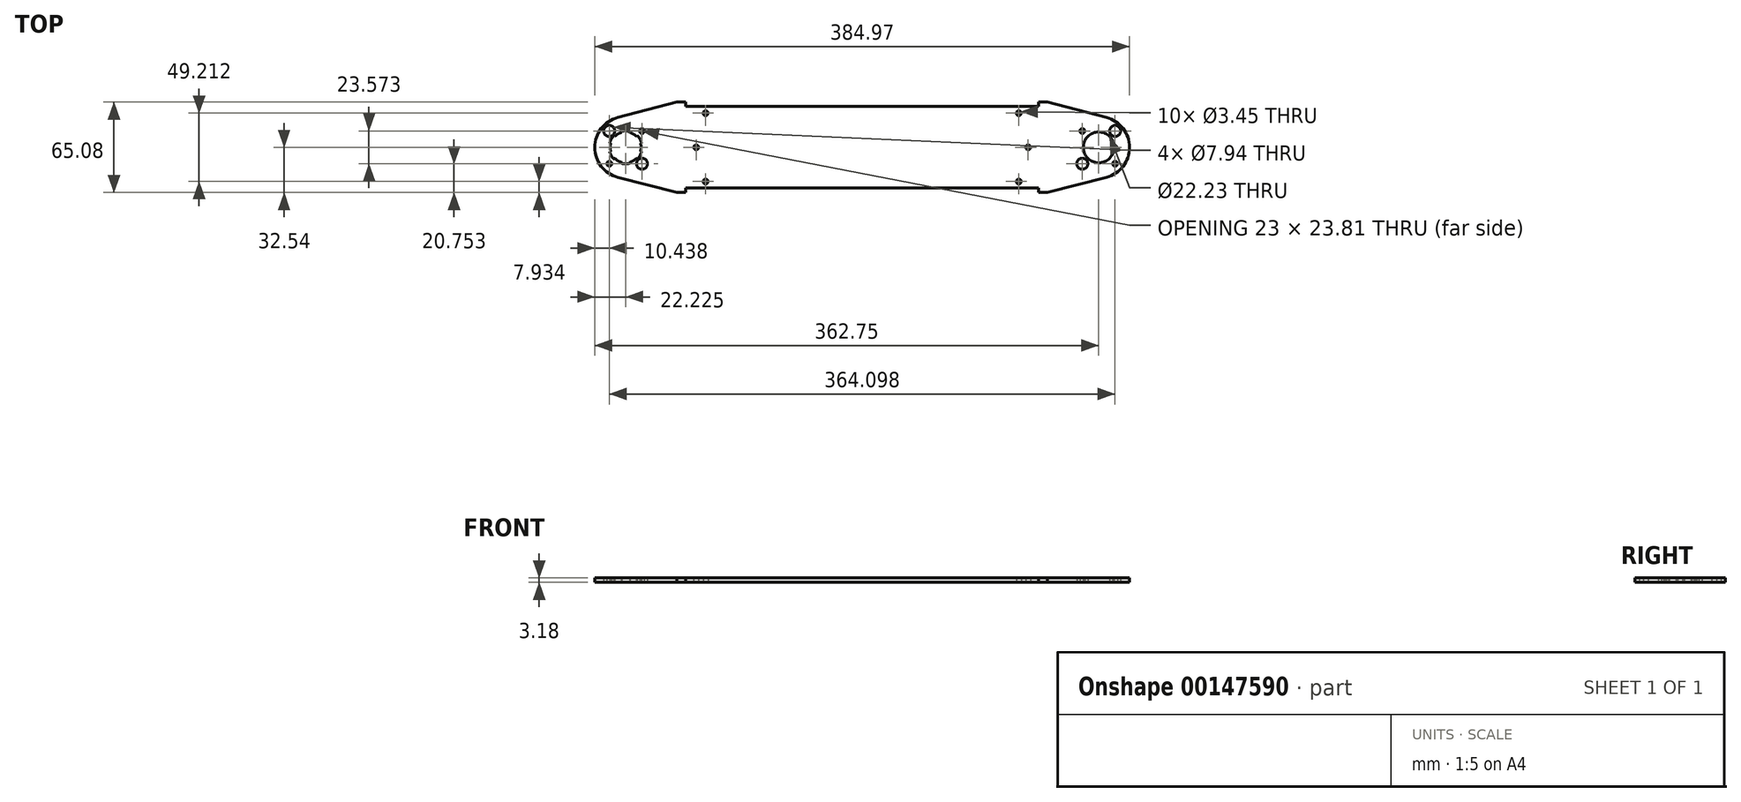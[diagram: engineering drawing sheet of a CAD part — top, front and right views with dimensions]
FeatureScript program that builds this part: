
annotation { "Feature Type Name" : "Feature", "Feature Type Description" : "" }
export const myFeature = defineFeature(function(context is Context, id is Id, definition is map)
    precondition{}
    {
        {
            var Q0;
            Q0=qCreatedBy(makeId("Top.planeOp"),FACE);
            var sketch = newSketch(context, id + "F0", { "sketchPlane" : qUnion([Q0])});
            skPoint(sketch, "E0.rect.middle", {"position": v(0, 0) * mm});
            skCircle(sketch, "E1", {"center": v(0, 0) * mm, "radius": 11.11 * mm});
            skLineSegment(sketch, "E2.bottom", {"start": v(11.79, 11.79) * mm, "end": v(-11.79, 11.79) * mm, "construction": true});
            skLineSegment(sketch, "E2.left", {"start": v(11.79, 11.79) * mm, "end": v(11.79, -11.79) * mm, "construction": true});
            skLineSegment(sketch, "E2.right", {"start": v(-11.79, 11.79) * mm, "end": v(-11.79, -11.79) * mm, "construction": true});
            skCircle(sketch, "E3", {"center": v(-11.79, 11.79) * mm, "radius": 1.73 * mm});
            skCircle(sketch, "E4", {"center": v(11.79, 11.79) * mm, "radius": 3.97 * mm});
            skCircle(sketch, "E5", {"center": v(11.79, -11.79) * mm, "radius": 1.73 * mm});
            skCircle(sketch, "E6", {"center": v(-11.79, -11.79) * mm, "radius": 3.97 * mm});
            skArc(sketch, "E7", {"start": v(-346.1, 21.51) * mm, "mid": v(-362.75, 0) * mm, "end": v(-346.1, -21.51) * mm});
            skLineSegment(sketch, "E8.bottom", {"start": v(-352.31, 11.79) * mm, "end": v(-328.74, 11.79) * mm, "construction": true});
            skLineSegment(sketch, "E8.top", {"start": v(-352.31, -11.79) * mm, "end": v(-328.74, -11.79) * mm, "construction": true});
            skLineSegment(sketch, "E8.left", {"start": v(-352.31, 11.79) * mm, "end": v(-352.31, -11.79) * mm, "construction": true});
            skLineSegment(sketch, "E8.right", {"start": v(-328.74, 11.79) * mm, "end": v(-328.74, -11.79) * mm, "construction": true});
            skCircle(sketch, "E9", {"center": v(-328.74, 11.79) * mm, "radius": 1.73 * mm});
            skCircle(sketch, "E10", {"center": v(-340.53, 0) * mm, "radius": 11.11 * mm});
            skCircle(sketch, "E11", {"center": v(-352.31, 11.79) * mm, "radius": 3.97 * mm});
            skCircle(sketch, "E12", {"center": v(-352.31, -11.79) * mm, "radius": 1.73 * mm});
            skCircle(sketch, "E13", {"center": v(-328.74, -11.79) * mm, "radius": 3.97 * mm});
            skLineSegment(sketch, "E14", {"start": v(0, 0) * mm, "end": v(-340.53, 0) * mm, "construction": true});
            skLineSegment(sketch, "E15", {"start": v(-346.1, -21.51) * mm, "end": v(-303.61, -32.54) * mm});
            skLineSegment(sketch, "E16", {"start": v(-346.1, 21.51) * mm, "end": v(-303.61, 32.54) * mm});
            skLineSegment(sketch, "E17", {"start": v(-297.26, -29.37) * mm, "end": v(-43.26, -29.37) * mm});
            skLineSegment(sketch, "E18", {"start": v(-297.26, 29.37) * mm, "end": v(-43.26, 29.37) * mm});
            skLineSegment(sketch, "E19", {"start": v(-297.26, 32.54) * mm, "end": v(-297.26, 29.37) * mm});
            skLineSegment(sketch, "E20", {"start": v(-297.26, 32.54) * mm, "end": v(-303.61, 32.54) * mm});
            skLineSegment(sketch, "E21", {"start": v(-297.26, -29.37) * mm, "end": v(-297.26, -32.54) * mm});
            skLineSegment(sketch, "E22", {"start": v(-297.26, -32.54) * mm, "end": v(-303.61, -32.54) * mm});
            skLineSegment(sketch, "E23", {"start": v(-43.26, -29.37) * mm, "end": v(-43.26, -32.54) * mm});
            skLineSegment(sketch, "E24", {"start": v(-43.26, -32.54) * mm, "end": v(-36.91, -32.54) * mm});
            skLineSegment(sketch, "E25", {"start": v(-43.26, 29.37) * mm, "end": v(-43.26, 32.54) * mm});
            skLineSegment(sketch, "E26", {"start": v(-43.26, 32.54) * mm, "end": v(-36.91, 32.54) * mm});
            skLineSegment(sketch, "E27", {"start": v(-36.91, -32.54) * mm, "end": v(5.58, -21.51) * mm});
            skLineSegment(sketch, "E28", {"start": v(5.58, 21.51) * mm, "end": v(-36.91, 32.54) * mm});
            skLineSegment(sketch, "E29", {"start": v(-297.26, 29.37) * mm, "end": v(-297.26, 24.6) * mm, "construction": true});
            skLineSegment(sketch, "E30", {"start": v(-297.26, 24.6) * mm, "end": v(-282.98, 24.6) * mm, "construction": true});
            skLineSegment(sketch, "E31", {"start": v(-297.26, -29.37) * mm, "end": v(-297.26, -24.6) * mm, "construction": true});
            skLineSegment(sketch, "E32", {"start": v(-297.26, -24.6) * mm, "end": v(-282.98, -24.6) * mm, "construction": true});
            skLineSegment(sketch, "E33", {"start": v(-43.26, -29.37) * mm, "end": v(-43.26, -24.6) * mm, "construction": true});
            skLineSegment(sketch, "E34", {"start": v(-43.26, -24.6) * mm, "end": v(-57.55, -24.6) * mm, "construction": true});
            skLineSegment(sketch, "E35", {"start": v(-43.26, 29.37) * mm, "end": v(-43.26, 24.6) * mm, "construction": true});
            skLineSegment(sketch, "E36", {"start": v(-43.26, 24.6) * mm, "end": v(-57.55, 24.6) * mm, "construction": true});
            skCircle(sketch, "E37", {"center": v(-282.98, 24.6) * mm, "radius": 1.73 * mm});
            skCircle(sketch, "E38", {"center": v(-57.55, 24.6) * mm, "radius": 1.73 * mm});
            skCircle(sketch, "E39", {"center": v(-57.55, -24.6) * mm, "radius": 1.73 * mm});
            skCircle(sketch, "E40", {"center": v(-282.98, -24.6) * mm, "radius": 1.73 * mm});
            skLineSegment(sketch, "E41", {"start": v(-11.79, -11.79) * mm, "end": v(11.79, -11.79) * mm, "construction": true});
            skLineSegment(sketch, "E42", {"start": v(-170.26, -29.37) * mm, "end": v(-170.26, 0) * mm, "construction": true});
            skLineSegment(sketch, "E43", {"start": v(-170.26, 0) * mm, "end": v(-170.26, 29.37) * mm, "construction": true});
            skArc(sketch, "E44", {"start": v(5.58, -21.51) * mm, "mid": v(22.23, 0) * mm, "end": v(5.58, 21.51) * mm});
            skLineSegment(sketch, "E45", {"start": v(-328.74, 11.79) * mm, "end": v(-289.73, 11.79) * mm, "construction": true});
            skLineSegment(sketch, "E46", {"start": v(-289.73, 11.79) * mm, "end": v(-289.73, 0) * mm, "construction": true});
            skLineSegment(sketch, "E47", {"start": v(-11.79, 11.79) * mm, "end": v(-50.8, 11.79) * mm, "construction": true});
            skLineSegment(sketch, "E48", {"start": v(-50.8, 11.79) * mm, "end": v(-50.8, 0) * mm, "construction": true});
            skCircle(sketch, "E49", {"center": v(-289.73, 0) * mm, "radius": 1.73 * mm});
            skCircle(sketch, "E50", {"center": v(-50.8, 0) * mm, "radius": 1.73 * mm});
            skSolve(sketch);
        }
        {
            var Q0;
            Q0=qSketchRegion(id+"F0",true);
            extrude(context, id + "F1", {"entities" : qUnion([Q0]), "depth" : 3.17 * mm});
        }
        {
            var Q0;
            Q0=makeQuery(id+"F1.opExtrude","CAP_FACE",FACE,{"disambiguationData":[OSD([sQuery(id+"F0.wireOp",EDGE,"d63eafa0-1946-4b0e-8293-95e246b273c5.rect.bottom"),sQuery(id+"F0.wireOp",EDGE,"d63eafa0-1946-4b0e-8293-95e246b273c5.rect.top"),sQuery(id+"F0.wireOp",EDGE,"5983dcdd-59a7-4b72-80fd-e4567be1ae8a"),sQuery(id+"F0.wireOp",EDGE,"5a538b3e-fc2b-4d64-affd-5d60433388e5"),sQuery(id+"F0.wireOp",EDGE,"72e86de7-b207-474f-aadf-64543fae3f9b"),sQuery(id+"F0.wireOp",EDGE,"1c038800-5bd5-4753-8b38-6da13ef78ef9"),sQuery(id+"F0.wireOp",EDGE,"EbMUZoU6-Ffds-1dNq-SxhE-hPi8oSjhvaod"),sQuery(id+"F0.wireOp",EDGE,"RfgQjzcw-1Izs-lnTa-bWkk-oBHRDQjbZqQC"),sQuery(id+"F0.wireOp",EDGE,"1cCQAcjj-TyQA-3DMx-kDix-v5yZVaaGeXVM"),sQuery(id+"F0.wireOp",EDGE,"7KPu8lni-3ZWA-t6oJ-FRoh-C5MB3aVr7E9B"),sQuery(id+"F0.wireOp",EDGE,"bSzr06ES-7M0i-Fw5H-UJmt-4e4EQGRPIe4n"),sQuery(id+"F0.wireOp",EDGE,"WGsr6OjU-OX8l-mawA-7cCc-MfOuMOY06Cp5"),sQuery(id+"F0.wireOp",EDGE,"9mrz1cDN-18gM-20ra-6VCO-jp25g10tvNn2"),sQuery(id+"F0.wireOp",EDGE,"G0uOisy3-Mq6h-PcKh-Zkf4-CVoCvP3Hii1l"),sQuery(id+"F0.wireOp",EDGE,"1ae556be-0ab9-4322-b48e-98cf5a741ae0"),sQuery(id+"F0.wireOp",EDGE,"676cd913-43f8-42b3-8cdc-a90136d19ef5"),sQuery(id+"F0.wireOp",EDGE,"xnt2EyF8-ZVyQ-RbWD-GIsP-ThkcyX8ZioIH.bottom"),sQuery(id+"F0.wireOp",EDGE,"xnt2EyF8-ZVyQ-RbWD-GIsP-ThkcyX8ZioIH.top"),sQuery(id+"F0.wireOp",EDGE,"xnt2EyF8-ZVyQ-RbWD-GIsP-ThkcyX8ZioIH.left"),sQuery(id+"F0.wireOp",EDGE,"E1"),sQuery(id+"F0.wireOp",EDGE,"Jo9pZc7T-t0kF-vjz1-dNbX-L65bwNqtrrdz"),sQuery(id+"F0.wireOp",EDGE,"lEYoY9t7-PMOS-SVp6-xfnB-Xp9WdWMCDdum"),sQuery(id+"F0.wireOp",EDGE,"s7aM02SC-9XQ7-dueL-DqMg-ZFuJqOofj9mt"),sQuery(id+"F0.wireOp",EDGE,"deKa9ngt-XMq2-GGkr-SZIa-KlyN0U5bcCDe"),sQuery(id+"F0.wireOp",EDGE,"E3"),sQuery(id+"F0.wireOp",EDGE,"E4"),sQuery(id+"F0.wireOp",EDGE,"E5"),sQuery(id+"F0.wireOp",EDGE,"E6"),sQuery(id+"F0.wireOp",EDGE,"E7"),sQuery(id+"F0.wireOp",EDGE,"E9"),sQuery(id+"F0.wireOp",EDGE,"E10"),sQuery(id+"F0.wireOp",EDGE,"E11"),sQuery(id+"F0.wireOp",EDGE,"E12"),sQuery(id+"F0.wireOp",EDGE,"E13")])],"isStart":true});
            var sketch = newSketch(context, id + "F2", { "sketchPlane" : qUnion([Q0])});
            skLineSegment(sketch, "E51", {"start": v(-340.53, 0) * mm, "end": v(-350.15, -5.56) * mm, "construction": true});
            skArc(sketch, "E52", {"start": v(-351.26, -2.88) * mm, "mid": v(-350.15, -5.56) * mm, "end": v(-348.38, -7.86) * mm});
            skLineSegment(sketch, "E53", {"start": v(-340.53, 0) * mm, "end": v(-348.38, -7.86) * mm, "construction": true});
            skLineSegment(sketch, "E54", {"start": v(-340.53, 0) * mm, "end": v(-351.26, -2.88) * mm, "construction": true});
            skLineSegment(sketch, "E55", {"start": v(-348.38, -7.86) * mm, "end": v(-348.94, -8.42) * mm});
            skLineSegment(sketch, "E56", {"start": v(-351.26, -2.88) * mm, "end": v(-352.03, -3.08) * mm});
            skArc(sketch, "E57", {"start": v(-352.03, -3.08) * mm, "mid": v(-350.84, -5.95) * mm, "end": v(-348.94, -8.42) * mm});
            skLineSegment(sketch, "E58", {"start": v(-340.53, 0) * mm, "end": v(-351.64, 0) * mm, "construction": true});
            skSolve(sketch);
        }
        {
            var Q0;
            Q0=qSketchRegion(id+"F2",true);
            var Q1;
            Q1=makeQuery(id+"F1.opExtrude","CAP_FACE",FACE,{"disambiguationData":[OSD([sQuery(id+"F0.wireOp",EDGE,"d63eafa0-1946-4b0e-8293-95e246b273c5.rect.bottom"),sQuery(id+"F0.wireOp",EDGE,"d63eafa0-1946-4b0e-8293-95e246b273c5.rect.top"),sQuery(id+"F0.wireOp",EDGE,"5983dcdd-59a7-4b72-80fd-e4567be1ae8a"),sQuery(id+"F0.wireOp",EDGE,"5a538b3e-fc2b-4d64-affd-5d60433388e5"),sQuery(id+"F0.wireOp",EDGE,"72e86de7-b207-474f-aadf-64543fae3f9b"),sQuery(id+"F0.wireOp",EDGE,"1c038800-5bd5-4753-8b38-6da13ef78ef9"),sQuery(id+"F0.wireOp",EDGE,"EbMUZoU6-Ffds-1dNq-SxhE-hPi8oSjhvaod"),sQuery(id+"F0.wireOp",EDGE,"RfgQjzcw-1Izs-lnTa-bWkk-oBHRDQjbZqQC"),sQuery(id+"F0.wireOp",EDGE,"1cCQAcjj-TyQA-3DMx-kDix-v5yZVaaGeXVM"),sQuery(id+"F0.wireOp",EDGE,"7KPu8lni-3ZWA-t6oJ-FRoh-C5MB3aVr7E9B"),sQuery(id+"F0.wireOp",EDGE,"bSzr06ES-7M0i-Fw5H-UJmt-4e4EQGRPIe4n"),sQuery(id+"F0.wireOp",EDGE,"WGsr6OjU-OX8l-mawA-7cCc-MfOuMOY06Cp5"),sQuery(id+"F0.wireOp",EDGE,"9mrz1cDN-18gM-20ra-6VCO-jp25g10tvNn2"),sQuery(id+"F0.wireOp",EDGE,"G0uOisy3-Mq6h-PcKh-Zkf4-CVoCvP3Hii1l"),sQuery(id+"F0.wireOp",EDGE,"1ae556be-0ab9-4322-b48e-98cf5a741ae0"),sQuery(id+"F0.wireOp",EDGE,"676cd913-43f8-42b3-8cdc-a90136d19ef5"),sQuery(id+"F0.wireOp",EDGE,"xnt2EyF8-ZVyQ-RbWD-GIsP-ThkcyX8ZioIH.bottom"),sQuery(id+"F0.wireOp",EDGE,"xnt2EyF8-ZVyQ-RbWD-GIsP-ThkcyX8ZioIH.top"),sQuery(id+"F0.wireOp",EDGE,"xnt2EyF8-ZVyQ-RbWD-GIsP-ThkcyX8ZioIH.left"),sQuery(id+"F0.wireOp",EDGE,"E1"),sQuery(id+"F0.wireOp",EDGE,"Jo9pZc7T-t0kF-vjz1-dNbX-L65bwNqtrrdz"),sQuery(id+"F0.wireOp",EDGE,"lEYoY9t7-PMOS-SVp6-xfnB-Xp9WdWMCDdum"),sQuery(id+"F0.wireOp",EDGE,"s7aM02SC-9XQ7-dueL-DqMg-ZFuJqOofj9mt"),sQuery(id+"F0.wireOp",EDGE,"deKa9ngt-XMq2-GGkr-SZIa-KlyN0U5bcCDe"),sQuery(id+"F0.wireOp",EDGE,"E3"),sQuery(id+"F0.wireOp",EDGE,"E4"),sQuery(id+"F0.wireOp",EDGE,"E5"),sQuery(id+"F0.wireOp",EDGE,"E6"),sQuery(id+"F0.wireOp",EDGE,"E7"),sQuery(id+"F0.wireOp",EDGE,"E9"),sQuery(id+"F0.wireOp",EDGE,"E10"),sQuery(id+"F0.wireOp",EDGE,"E11"),sQuery(id+"F0.wireOp",EDGE,"E12"),sQuery(id+"F0.wireOp",EDGE,"E13")])],"isStart":false});
            extrude(context, id + "F3", {"entities" : qUnion([Q0]), "operationType" : NewBodyOperationType.REMOVE, "endBound" : BoundingType.UP_TO_SURFACE, "oppositeDirection" : true, "endBoundEntityFace" : qUnion([Q1]), "depth" : 25.4 * mm});
        }
        {
            var Q0;
            Q0=makeQuery(id+"F3.boolean.opBoolean","COPY",FACE,{"derivedFrom":makeQuery(id+"F3.opExtrude","SWEPT_FACE",FACE,{"disambiguationData":[OSD([sQuery(id+"F2.wireOp",EDGE,"E55")])]})});
            var Q1;
            Q1=makeQuery(id+"F3.boolean.opBoolean","COPY",FACE,{"derivedFrom":makeQuery(id+"F3.opExtrude","SWEPT_FACE",FACE,{"disambiguationData":[OSD([sQuery(id+"F2.wireOp",EDGE,"E57")])]})});
            var Q2;
            Q2=makeQuery(id+"F3.boolean.opBoolean","COPY",FACE,{"derivedFrom":makeQuery(id+"F3.opExtrude","SWEPT_FACE",FACE,{"disambiguationData":[OSD([sQuery(id+"F2.wireOp",EDGE,"E56")])]})});
            var Q3;
            Q3=makeQuery(id+"F1.opExtrude","SWEPT_FACE",FACE,{"disambiguationData":[OSD([sQuery(id+"F0.wireOp",EDGE,"E10")])]});
            circularPattern(context, id + "F4", {"patternType" : PatternType.FACE, "faces" : qUnion([Q0, Q1, Q2]), "axis" : qUnion([Q3]), "angle" : 60 * degree, "instanceCount" : 6});
        }
    });
